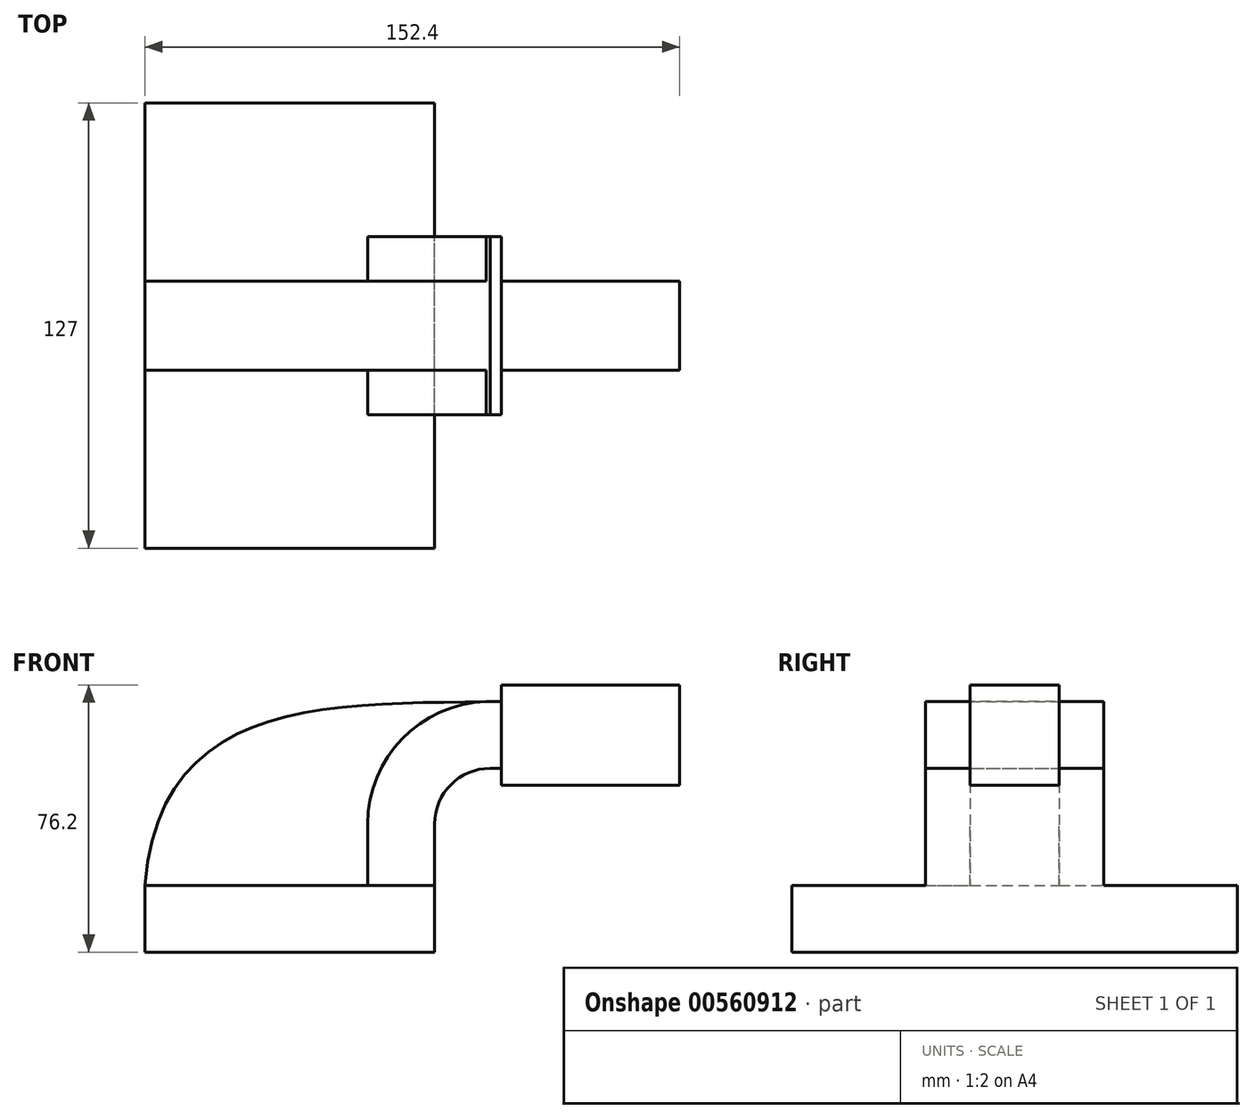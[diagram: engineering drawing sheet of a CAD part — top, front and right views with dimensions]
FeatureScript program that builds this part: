
annotation { "Feature Type Name" : "Feature", "Feature Type Description" : "" }
export const myFeature = defineFeature(function(context is Context, id is Id, definition is map)
    precondition{}
    {
        {
            var Q0;
            Q0=qCreatedBy(makeId("Front.planeOp"),FACE);
            var sketch = newSketch(context, id + "F0", { "sketchPlane" : qUnion([Q0])});
            skLineSegment(sketch, "E0.bottom", {"start": v(-41.28, 12.74) * mm, "end": v(41.28, 12.74) * mm});
            skLineSegment(sketch, "E0.top", {"start": v(-41.28, -6.3) * mm, "end": v(41.28, -6.3) * mm});
            skLineSegment(sketch, "E0.left", {"start": v(-41.28, 12.74) * mm, "end": v(-41.28, -6.3) * mm});
            skLineSegment(sketch, "E0.right", {"start": v(41.28, 12.74) * mm, "end": v(41.28, -6.3) * mm});
            skPoint(sketch, "E0.middle", {"position": v(0, 3.22) * mm});
            skLineSegment(sketch, "E1.bottom", {"start": v(60.32, 69.9) * mm, "end": v(111.12, 69.9) * mm});
            skLineSegment(sketch, "E1.top", {"start": v(60.33, 41.32) * mm, "end": v(111.12, 41.32) * mm});
            skLineSegment(sketch, "E1.left", {"start": v(60.32, 69.9) * mm, "end": v(60.33, 41.32) * mm});
            skLineSegment(sketch, "E1.right", {"start": v(111.13, 69.9) * mm, "end": v(111.13, 41.32) * mm});
            skPoint(sketch, "E1.middle", {"position": v(85.73, 55.6) * mm});
            skLineSegment(sketch, "E2", {"start": v(41.28, 12.74) * mm, "end": v(41.28, 30.22) * mm});
            skArc(sketch, "E3", {"start": v(41.28, 30.22) * mm, "mid": v(45.92, 41.44) * mm, "end": v(57.15, 46.1) * mm});
            skLineSegment(sketch, "E4", {"start": v(57.15, 46.1) * mm, "end": v(93.53, 46.1) * mm});
            skLineSegment(sketch, "E5.0", {"start": v(57.15, 65.14) * mm, "end": v(93.53, 65.14) * mm});
            skArc(sketch, "E5.1", {"start": v(22.23, 30.22) * mm, "mid": v(32.45, 54.91) * mm, "end": v(57.15, 65.14) * mm});
            skLineSegment(sketch, "E5.2", {"start": v(22.23, 12.74) * mm, "end": v(22.23, 30.22) * mm});
            skLineSegment(sketch, "E6", {"start": v(93.53, 41.32) * mm, "end": v(93.53, 69.9) * mm});
            skFitSpline(sketch, "E7", {"points": [v(57.15, 65.14) * mm, v(-41.28, 12.74) * mm], "startDerivative": vector(-139.65, -2.37) * mm, "endDerivative": vector(-13.1, -161.31) * mm});
            skSolve(sketch);
        }
        {
            var Q0;
            Q0=makeQuery(id+"F0.imprint","IMPRINT",FACE,{"disambiguationData":[TD([[makeQuery(id+"F0.imprint","IMPRINT",EDGE,{"derivedFrom":sQuery(id+"F0.wireOp",EDGE,"E0.top")}),1.0]])]});
            extrude(context, id + "F1", {"entities" : qUnion([Q0]), "endBound" : BoundingType.SYMMETRIC, "depth" : 127 * mm, "offsetDistance" : 25.4 * mm});
        }
        {
            var Q0;
            {var subQ6=sQuery(id+"F0.wireOp",EDGE,"E2");Q0=makeQuery(id+"F0.imprint","IMPRINT",FACE,{"disambiguationData":[TD([[makeQuery(id+"F0.imprint","IMPRINT",EDGE,{"derivedFrom":subQ6}),1.0]])]});}
            extrude(context, id + "F2", {"entities" : qUnion([Q0]), "operationType" : NewBodyOperationType.ADD, "endBound" : BoundingType.SYMMETRIC, "depth" : 50.8 * mm, "offsetDistance" : 25.4 * mm});
        }
        {
            var Q0;
            Q0 = qSketchRegion(id + "F0", true);
            extrude(context, id + "F3", {"entities" : qUnion([Q0]), "operationType" : NewBodyOperationType.ADD, "endBound" : BoundingType.SYMMETRIC, "depth" : 25.4 * mm, "offsetDistance" : 25.4 * mm});
        }
    });
